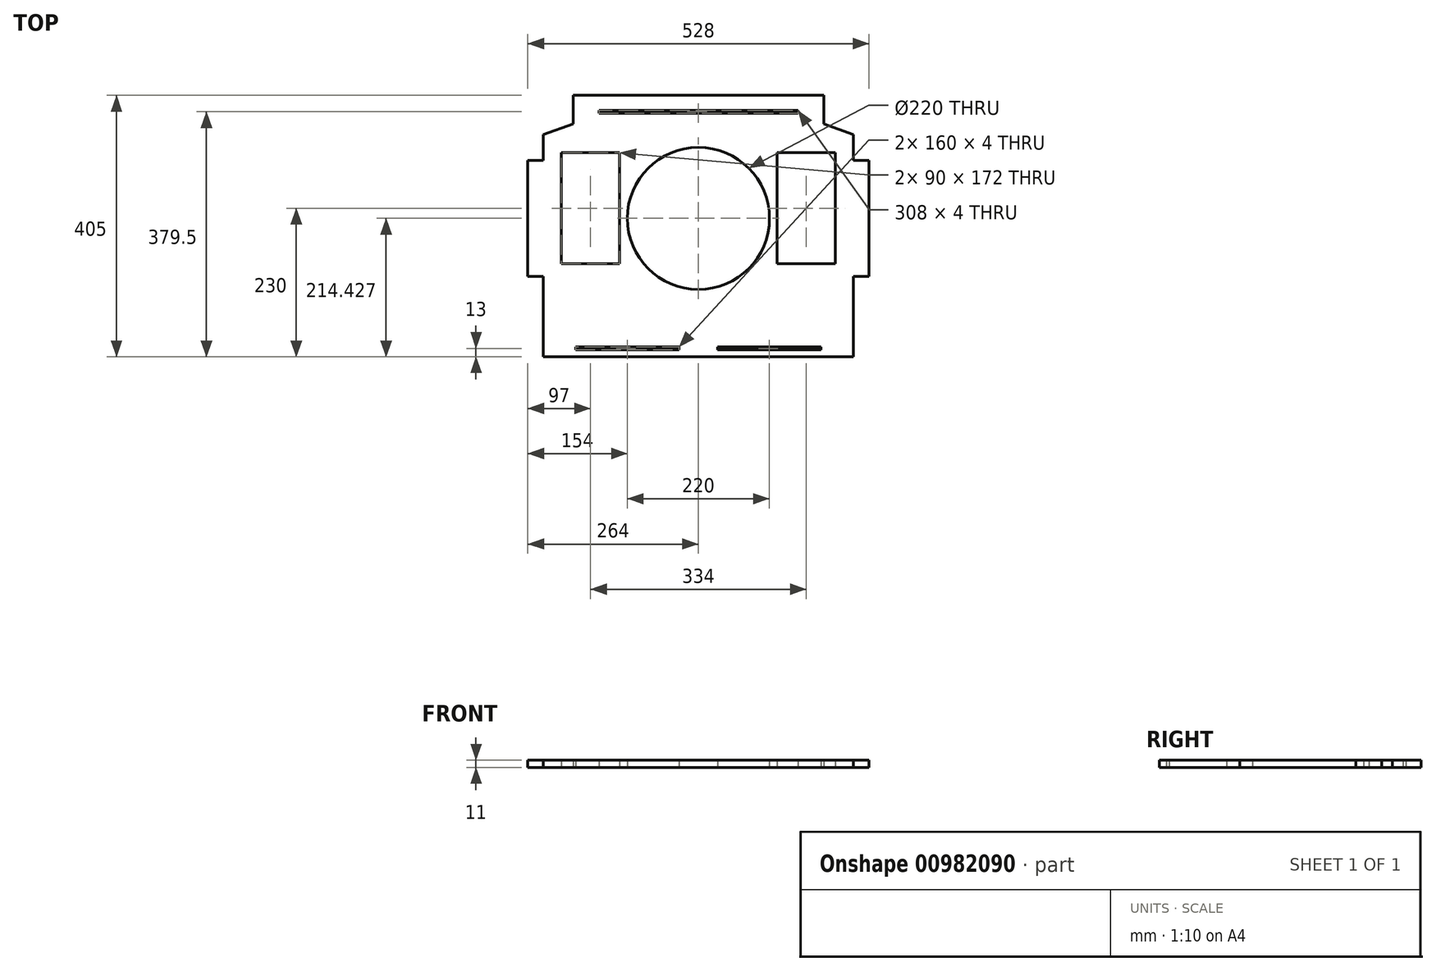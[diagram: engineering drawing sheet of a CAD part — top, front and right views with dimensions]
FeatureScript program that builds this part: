
annotation { "Feature Type Name" : "Feature", "Feature Type Description" : "" }
export const myFeature = defineFeature(function(context is Context, id is Id, definition is map)
    precondition{}
    {
        {
            var Q0;
            Q0=qCreatedBy(makeId("Top.planeOp"),FACE);
            var sketch = newSketch(context, id + "F0", { "sketchPlane" : qUnion([Q0])});
            skLineSegment(sketch, "E0", {"start": v(-194, 158.5) * mm, "end": v(-194, 202.5) * mm});
            skLineSegment(sketch, "E1", {"start": v(-154, 175) * mm, "end": v(-154, 179) * mm});
            skLineSegment(sketch, "E2", {"start": v(194, 158.5) * mm, "end": v(194, 202.5) * mm});
            skLineSegment(sketch, "E3", {"start": v(154, 175) * mm, "end": v(154, 179) * mm});
            skCircle(sketch, "E4", {"center": v(0, 11.93) * mm, "radius": 110 * mm});
            skLineSegment(sketch, "E5", {"start": v(240, 101.93) * mm, "end": v(240, 141.93) * mm});
            skLineSegment(sketch, "E6", {"start": v(264, -78.07) * mm, "end": v(264, 101.93) * mm});
            skLineSegment(sketch, "E7", {"start": v(240, 101.93) * mm, "end": v(264, 101.93) * mm});
            skLineSegment(sketch, "E8", {"start": v(194, 158.5) * mm, "end": v(240, 141.93) * mm});
            skLineSegment(sketch, "E9", {"start": v(-240, 101.93) * mm, "end": v(-240, 141.93) * mm});
            skLineSegment(sketch, "E10", {"start": v(-264, -78.07) * mm, "end": v(-264, 101.93) * mm});
            skLineSegment(sketch, "E11", {"start": v(-240, 101.93) * mm, "end": v(-264, 101.93) * mm});
            skLineSegment(sketch, "E12", {"start": v(-194, 158.5) * mm, "end": v(-240, 141.93) * mm});
            skLineSegment(sketch, "E13", {"start": v(-240, -78.07) * mm, "end": v(-264, -78.07) * mm});
            skLineSegment(sketch, "E14", {"start": v(264, -78.07) * mm, "end": v(240, -78.07) * mm});
            skLineSegment(sketch, "E15", {"start": v(-240, -202.5) * mm, "end": v(240, -202.5) * mm});
            skLineSegment(sketch, "E16", {"start": v(-190, -187.5) * mm, "end": v(-30, -187.5) * mm});
            skLineSegment(sketch, "E17", {"start": v(30, -187.5) * mm, "end": v(190, -187.5) * mm});
            skLineSegment(sketch, "E18", {"start": v(-190, -191.5) * mm, "end": v(-30, -191.5) * mm});
            skLineSegment(sketch, "E19", {"start": v(30, -191.5) * mm, "end": v(190, -191.5) * mm});
            skLineSegment(sketch, "E20", {"start": v(-194, 202.5) * mm, "end": v(194, 202.5) * mm});
            skLineSegment(sketch, "E21", {"start": v(-154, 175) * mm, "end": v(154, 175) * mm});
            skLineSegment(sketch, "E22", {"start": v(-154, 179) * mm, "end": v(154, 179) * mm});
            skLineSegment(sketch, "E23", {"start": v(-240, -78.07) * mm, "end": v(-240, -202.5) * mm});
            skLineSegment(sketch, "E24", {"start": v(-190, -187.5) * mm, "end": v(-190, -191.5) * mm});
            skLineSegment(sketch, "E25", {"start": v(240, -78.07) * mm, "end": v(240, -202.5) * mm});
            skLineSegment(sketch, "E26", {"start": v(190, -187.5) * mm, "end": v(190, -191.5) * mm});
            skLineSegment(sketch, "E27", {"start": v(-122, -58.5) * mm, "end": v(-212, -58.5) * mm});
            skLineSegment(sketch, "E28", {"start": v(-122, 113.5) * mm, "end": v(-212, 113.5) * mm});
            skLineSegment(sketch, "E29", {"start": v(-122, 113.5) * mm, "end": v(-122, -58.5) * mm});
            skLineSegment(sketch, "E30", {"start": v(-212, 113.5) * mm, "end": v(-212, -58.5) * mm});
            skLineSegment(sketch, "E31", {"start": v(-30, -191.5) * mm, "end": v(-30, -187.5) * mm});
            skLineSegment(sketch, "E32", {"start": v(30, -191.5) * mm, "end": v(30, -187.5) * mm});
            skLineSegment(sketch, "E33", {"start": v(122, -58.5) * mm, "end": v(212, -58.5) * mm});
            skLineSegment(sketch, "E34", {"start": v(122, 113.5) * mm, "end": v(212, 113.5) * mm});
            skLineSegment(sketch, "E35", {"start": v(122, 113.5) * mm, "end": v(122, -58.5) * mm});
            skLineSegment(sketch, "E36", {"start": v(212, 113.5) * mm, "end": v(212, -58.5) * mm});
            skSolve(sketch);
        }
        {
            var Q0;
            Q0=makeQuery(id+"F0.imprint","IMPRINT",FACE,{"disambiguationData":[TD([[makeQuery(id+"F0.imprint","IMPRINT",EDGE,{"derivedFrom":sQuery(id+"F0.wireOp",EDGE,"E0")}),-1.0]])]});
            extrude(context, id + "F1", {"entities" : qUnion([Q0]), "depth" : 11 * mm, "offsetDistance" : 25 * mm});
        }
        {
            var Q0;
            Q0=makeQuery(id+"F1.opExtrude","SWEPT_FACE",FACE,{"disambiguationData":[OSD([sQuery(id+"F0.wireOp",EDGE,"E35")])]});
            cPlane(context, id + "F2", {"entities" : qUnion([Q0]), "cplaneType" : CPlaneType.OFFSET, "offset" : 45 * mm, "width" : 150 * mm, "height" : 150 * mm});
        }
    });
